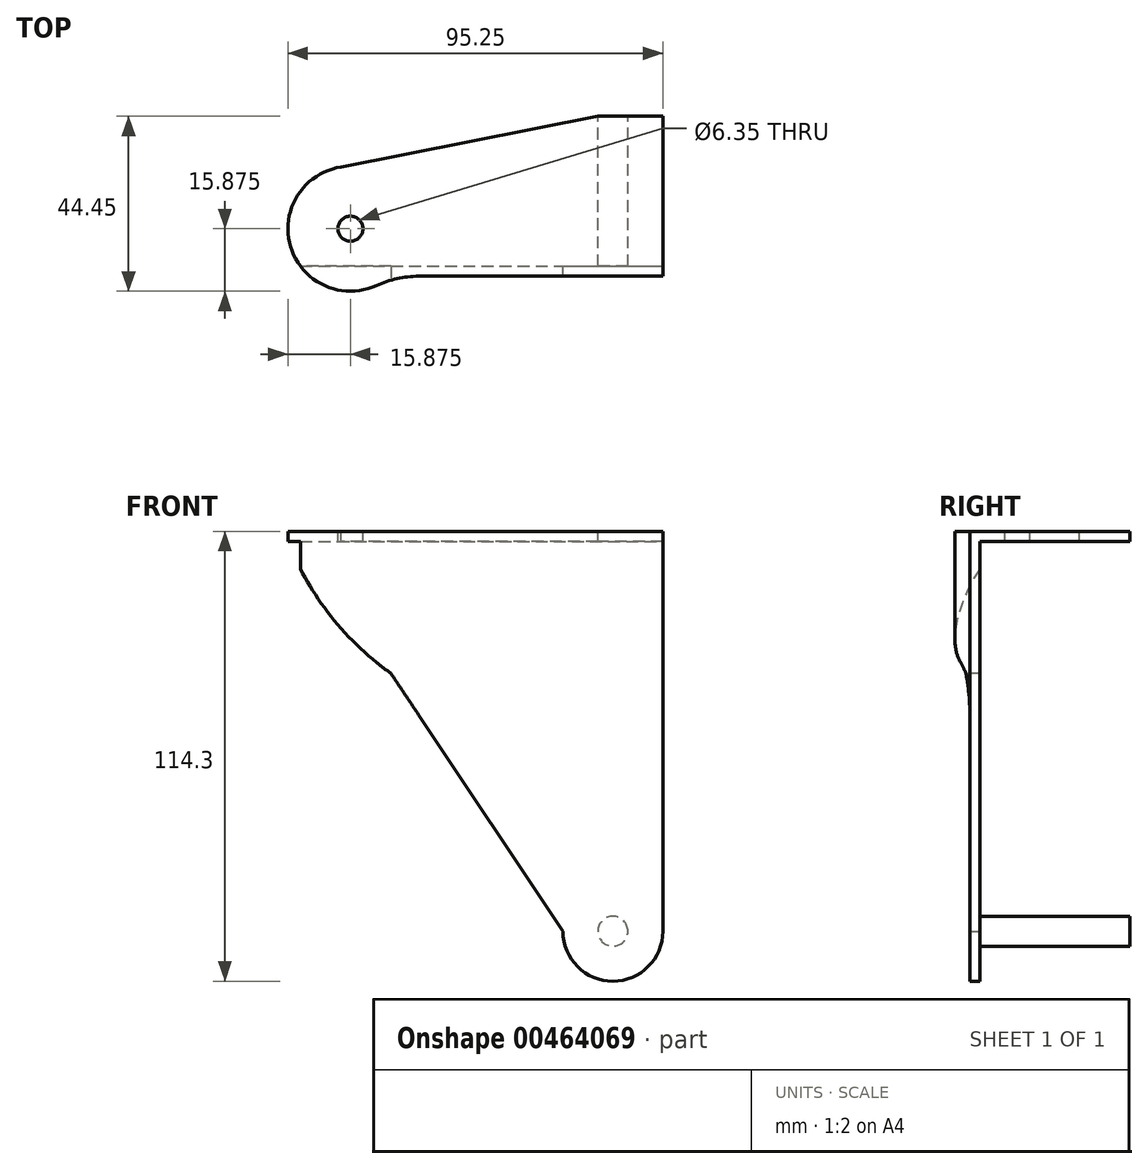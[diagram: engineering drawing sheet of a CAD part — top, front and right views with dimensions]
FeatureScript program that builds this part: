
annotation { "Feature Type Name" : "Feature", "Feature Type Description" : "" }
export const myFeature = defineFeature(function(context is Context, id is Id, definition is map)
    precondition{}
    {
        {
            var Q0;
            Q0=qCreatedBy(makeId("Front.planeOp"),FACE);
            var sketch = newSketch(context, id + "F0", { "sketchPlane" : qUnion([Q0])});
            skCircle(sketch, "E0", {"center": v(0, 0) * mm, "radius": 3.81 * mm});
            skSolve(sketch);
        }
        {
            var Q0;
            Q0 = qSketchRegion(id + "F0", true);
            extrude(context, id + "F1", {"entities" : qUnion([Q0]), "depth" : 38.1 * mm, "offsetDistance" : 25.4 * mm});
        }
        {
            var Q0;
            Q0=makeQuery(id+"F1.opExtrude","CAP_FACE",FACE,{"disambiguationData":[OSD([sQuery(id+"F0.wireOp",EDGE,"E0")])],"isStart":false});
            var sketch = newSketch(context, id + "F2", { "sketchPlane" : qUnion([Q0])});
            skCircle(sketch, "E1", {"center": v(0, 0) * mm, "radius": 12.7 * mm});
            skLineSegment(sketch, "E2", {"start": v(-63.5, 76.2) * mm, "end": v(-12.7, 0) * mm});
            skLineSegment(sketch, "E3", {"start": v(-63.5, 76.2) * mm, "end": v(-63.5, 101.6) * mm});
            skLineSegment(sketch, "E4", {"start": v(0, 0) * mm, "end": v(12.7, 0) * mm});
            skLineSegment(sketch, "E5", {"start": v(12.7, 0) * mm, "end": v(12.7, 101.6) * mm});
            skLineSegment(sketch, "E6", {"start": v(-63.5, 101.6) * mm, "end": v(12.7, 101.6) * mm});
            skSolve(sketch);
        }
        {
            var Q0;
            Q0 = qSketchRegion(id + "F2", true);
            extrude(context, id + "F3", {"entities" : qUnion([Q0]), "operationType" : NewBodyOperationType.ADD, "depth" : 2.54 * mm, "offsetDistance" : 25.4 * mm});
        }
        {
            var Q0;
            Q0=makeQuery(id+"F3.opExtrude","SWEPT_FACE",FACE,{"disambiguationData":[OSD([sQuery(id+"F2.wireOp",EDGE,"E6")])]});
            var sketch = newSketch(context, id + "F4", { "sketchPlane" : qUnion([Q0])});
            skLineSegment(sketch, "E7", {"start": v(0, 0) * mm, "end": v(-50.8, 0) * mm});
            skLineSegment(sketch, "E8", {"start": v(-50.8, 0) * mm, "end": v(-50.8, -19.05) * mm});
            skLineSegment(sketch, "E9", {"start": v(-50.8, -19.05) * mm, "end": v(-50.8, -28.58) * mm});
            skLineSegment(sketch, "E10", {"start": v(-50.8, -28.58) * mm, "end": v(-57.15, -28.58) * mm});
            skLineSegment(sketch, "E11", {"start": v(-57.15, -28.58) * mm, "end": v(-63.5, -28.58) * mm});
            skLineSegment(sketch, "E12", {"start": v(-63.5, -28.58) * mm, "end": v(-69.85, -28.58) * mm});
            skCircle(sketch, "E13", {"center": v(-66.67, -28.58) * mm, "radius": 15.88 * mm});
            skSolve(sketch);
        }
        {
            var Q0;
            Q0 = qSketchRegion(id + "F4", true);
            extrude(context, id + "F5", {"entities" : qUnion([Q0]), "operationType" : NewBodyOperationType.ADD, "oppositeDirection" : true, "depth" : 57.9 * mm, "offsetDistance" : 25.4 * mm});
        }
        {
            var Q0;
            Q0=makeQuery(id+"F3.opExtrude","CAP_FACE",FACE,{"disambiguationData":[OSD([sQuery(id+"F2.wireOp",EDGE,"E1"),sQuery(id+"F2.wireOp",EDGE,"E2"),sQuery(id+"F2.wireOp",EDGE,"E3"),sQuery(id+"F2.wireOp",EDGE,"E5"),sQuery(id+"F2.wireOp",EDGE,"E6")])],"isStart":false});
            var sketch = newSketch(context, id + "F6", { "sketchPlane" : qUnion([Q0])});
            skLineSegment(sketch, "E14", {"start": v(-56.36, 65.49) * mm, "end": v(-56.36, 101.6) * mm});
            skLineSegment(sketch, "E15", {"start": v(-12.7, 0) * mm, "end": v(-56.36, 65.49) * mm});
            skLineSegment(sketch, "E16", {"start": v(-44.45, -6.5) * mm, "end": v(-12.7, 0) * mm});
            skLineSegment(sketch, "E17", {"start": v(-88.4, 14.16) * mm, "end": v(-84.61, 105.05) * mm});
            skLineSegment(sketch, "E18", {"start": v(-88.4, 14.16) * mm, "end": v(-44.45, -6.5) * mm});
            skArc(sketch, "E19", {"start": v(-84.61, 105.05) * mm, "mid": v(-73.8, 82.9) * mm, "end": v(-56.36, 65.49) * mm});
            skSolve(sketch);
        }
        {
            var Q0;
            Q0 = qSketchRegion(id + "F6", true);
            extrude(context, id + "F7", {"entities" : qUnion([Q0]), "operationType" : NewBodyOperationType.REMOVE, "oppositeDirection" : true, "depth" : 40.64 * mm, "offsetDistance" : 25.4 * mm, "hasSecondDirection" : true, "secondDirectionOppositeDirection" : false, "secondDirectionDepth" : 30.99 * mm});
        }
        {
            var Q0;
            Q0=makeQuery(id+"F3.opExtrude","SWEPT_FACE",FACE,{"disambiguationData":[OSD([sQuery(id+"F2.wireOp",EDGE,"E5")])]});
            var sketch = newSketch(context, id + "F8", { "sketchPlane" : qUnion([Q0])});
            skLineSegment(sketch, "E20", {"start": v(-6.17, 63.5) * mm, "end": v(-6.17, 4.69) * mm});
            skLineSegment(sketch, "E21", {"start": v(-6.17, 4.69) * mm, "end": v(-38.1, 4.69) * mm});
            skLineSegment(sketch, "E22", {"start": v(-38.1, 4.69) * mm, "end": v(-38.1, 101.6) * mm});
            skLineSegment(sketch, "E23", {"start": v(-38.1, 101.6) * mm, "end": v(-38.1, 99.06) * mm});
            skLineSegment(sketch, "E24", {"start": v(-38.1, 99.06) * mm, "end": v(-6.17, 99.06) * mm});
            skLineSegment(sketch, "E25", {"start": v(-6.17, 63.5) * mm, "end": v(-6.17, 99.06) * mm});
            skSolve(sketch);
        }
        {
            var Q0;
            Q0 = qSketchRegion(id + "F8", true);
            extrude(context, id + "F9", {"entities" : qUnion([Q0]), "operationType" : NewBodyOperationType.REMOVE, "oppositeDirection" : true, "depth" : 140.72 * mm, "offsetDistance" : 25.4 * mm});
        }
        {
            var Q0;
            Q0=makeQuery(id+"F5.boolean.opBoolean","MERGE",FACE,{"derivedFrom":[makeQuery(id+"F3.opExtrude","SWEPT_FACE",FACE,{"disambiguationData":[OSD([sQuery(id+"F2.wireOp",EDGE,"E6")])]}),makeQuery(id+"F5.opExtrude","CAP_FACE",FACE,{"disambiguationData":[OSD([sQuery(id+"F4.wireOp",EDGE,"E13")])],"isStart":true})]});
            var sketch = newSketch(context, id + "F10", { "sketchPlane" : qUnion([Q0])});
            skLineSegment(sketch, "E26", {"start": v(12.7, -38.1) * mm, "end": v(12.7, 0) * mm});
            skLineSegment(sketch, "E27", {"start": v(12.7, 0) * mm, "end": v(-3.8, 0) * mm});
            skLineSegment(sketch, "E28", {"start": v(-3.8, 0) * mm, "end": v(-70.5, -13.17) * mm});
            skSolve(sketch);
        }
        {
            var Q0;
            Q0=makeQuery(id+"F10.imprint","IMPRINT",FACE,{"disambiguationData":[TD([[makeQuery(id+"F10.imprint","IMPRINT",EDGE,{"derivedFrom":sQuery(id+"F10.wireOp",EDGE,"E26")}),1.0]])]});
            extrude(context, id + "F11", {"entities" : qUnion([Q0]), "operationType" : NewBodyOperationType.ADD, "oppositeDirection" : true, "depth" : 2.54 * mm, "offsetDistance" : 25.4 * mm});
        }
        {
            var Q0;
            Q0=makeQuery(id+"F5.boolean.opBoolean","INTERSECT",EDGE,{"derivedFrom":[makeQuery(id+"F3.opExtrude","CAP_FACE",FACE,{"disambiguationData":[OSD([sQuery(id+"F2.wireOp",EDGE,"E1"),sQuery(id+"F2.wireOp",EDGE,"E2"),sQuery(id+"F2.wireOp",EDGE,"E3"),sQuery(id+"F2.wireOp",EDGE,"E5"),sQuery(id+"F2.wireOp",EDGE,"E6")])],"isStart":false}),makeQuery(id+"F5.opExtrude","SWEPT_FACE",FACE,{"disambiguationData":[OSD([sQuery(id+"F4.wireOp",EDGE,"E13")])]})]});
            fillet(context, id + "F12", {"entities" : qUnion([Q0]), "radius" : 25.4 * mm, "tangentPropagation" : true, "allowEdgeOverflow" : false});
        }
        {
            var Q0;
            {var subQ0=sQuery(id+"F4.wireOp",EDGE,"E13");var subQ1=sQuery(id+"F2.wireOp",EDGE,"E6");Q0=makeQuery(id+"F11.boolean.opBoolean","MERGE",FACE,{"derivedFrom":[makeQuery(id+"F5.boolean.opBoolean","MERGE",FACE,{"derivedFrom":[makeQuery(id+"F3.opExtrude","SWEPT_FACE",FACE,{"disambiguationData":[OSD([subQ1])]}),makeQuery(id+"F5.opExtrude","CAP_FACE",FACE,{"disambiguationData":[OSD([subQ0])],"isStart":true})]}),makeQuery(id+"F11.opExtrude","CAP_FACE",FACE,{"disambiguationData":[OSD([subQ1,subQ0,sQuery(id+"F10.wireOp",EDGE,"E26"),sQuery(id+"F10.wireOp",EDGE,"E27"),sQuery(id+"F10.wireOp",EDGE,"E28")])],"isStart":true})]});}
            var sketch = newSketch(context, id + "F13", { "sketchPlane" : qUnion([Q0])});
            skCircle(sketch, "E29", {"center": v(-66.67, -28.58) * mm, "radius": 3.18 * mm});
            skSolve(sketch);
        }
        {
            var Q0;
            Q0 = qSketchRegion(id + "F13", true);
            extrude(context, id + "F14", {"entities" : qUnion([Q0]), "operationType" : NewBodyOperationType.REMOVE, "oppositeDirection" : true, "depth" : 25.4 * mm, "offsetDistance" : 25.4 * mm});
        }
    });
